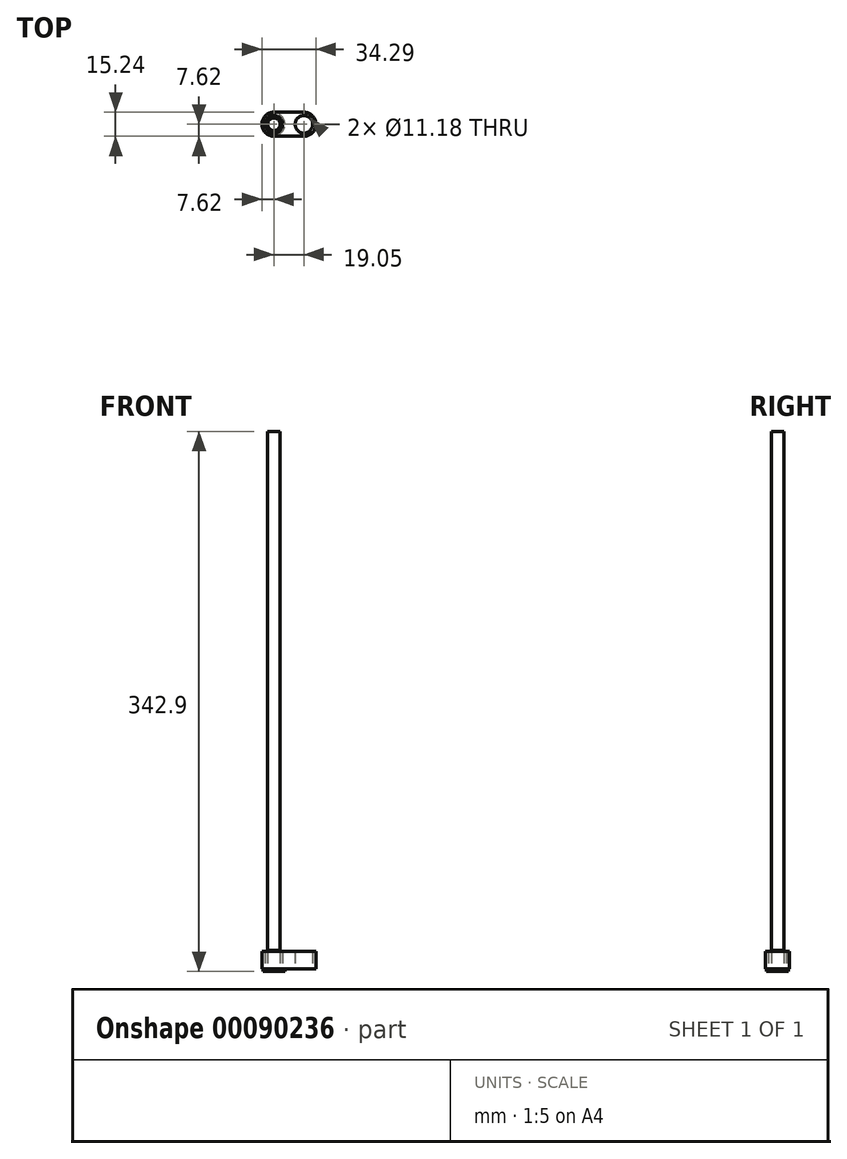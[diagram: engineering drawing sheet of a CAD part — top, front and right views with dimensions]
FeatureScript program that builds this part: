
annotation { "Feature Type Name" : "Feature", "Feature Type Description" : "" }
export const myFeature = defineFeature(function(context is Context, id is Id, definition is map)
    precondition{}
    {
        {
            assignVariable(context, id + "F0", {"name" : "AT", "anyValue" : 0.22});
        }
        {
            var Q0;
            Q0=qCreatedBy(makeId("Top.planeOp"),FACE);
            var sketch = newSketch(context, id + "F1", { "sketchPlane" : qUnion([Q0])});
            skCircle(sketch, "E0", {"center": v(0, 0) * mm, "radius": 3.97 * mm});
            skSolve(sketch);
        }
        {
            var Q0;
            Q0 = qSketchRegion(id + "F1", true);
            extrude(context, id + "F2", {"entities" : qUnion([Q0]), "depth" : 342.9 * mm});
        }
        {
            var Q0;
            Q0=qCreatedBy(makeId("Top.planeOp"),FACE);
            var sketch = newSketch(context, id + "F3", { "sketchPlane" : qUnion([Q0])});
            skCircle(sketch, "E1.0", {"center": v(0, 0) * mm, "radius": 3.97 * mm});
            skCircle(sketch, "E2", {"center": v(0, 0) * mm, "radius": 6.99 * mm});
            skSolve(sketch);
        }
        {
            var Q0;
            Q0=makeQuery(id+"F3.imprint","IMPRINT",FACE,{"disambiguationData":[TD([[makeQuery(id+"F3.imprint","IMPRINT",EDGE,{"derivedFrom":sQuery(id+"F3.wireOp",EDGE,"E1.0")}),-1.0]])]});
            extrude(context, id + "F4", {"entities" : qUnion([Q0]), "depth" : 1.57 * mm});
        }
        {
            var Q0;
            Q0=makeQuery(id+"F4.opExtrude","CAP_FACE",FACE,{"disambiguationData":[OSD([sQuery(id+"F3.wireOp",EDGE,"E1.0"),sQuery(id+"F3.wireOp",EDGE,"E2")])],"isStart":false});
            var sketch = newSketch(context, id + "F5", { "sketchPlane" : qUnion([Q0])});
            skCircle(sketch, "E3.0.0", {"center": v(0, 0) * mm, "radius": 6.99 * mm});
            skCircle(sketch, "E4", {"center": v(0, 0) * mm, "radius": 5.56 * mm});
            skSolve(sketch);
        }
        {
            var Q0;
            Q0=makeQuery(id+"F5.imprint","IMPRINT",FACE,{"disambiguationData":[TD([[makeQuery(id+"F5.imprint","IMPRINT",EDGE,{"derivedFrom":sQuery(id+"F5.wireOp",EDGE,"E4")}),1.0]])]});
            extrude(context, id + "F6", {"entities" : qUnion([Q0]), "operationType" : NewBodyOperationType.ADD, "depth" : 11.05 * mm});
        }
        {
            var Q0;
            Q0=makeQuery(id+"F4.opExtrude","CAP_FACE",FACE,{"disambiguationData":[OSD([sQuery(id+"F3.wireOp",EDGE,"E1.0"),sQuery(id+"F3.wireOp",EDGE,"E2")])],"isStart":false});
            var sketch = newSketch(context, id + "F7", { "sketchPlane" : qUnion([Q0])});
            skCircle(sketch, "E5.0", {"center": v(0, 0) * mm, "radius": 5.56 * mm});
            skCircle(sketch, "E6", {"center": v(0, 0) * mm, "radius": 7.62 * mm});
            skCircle(sketch, "E7", {"center": v(19.05, 0) * mm, "radius": 5.59 * mm});
            skCircle(sketch, "E8", {"center": v(19.05, 0) * mm, "radius": 7.62 * mm});
            skLineSegment(sketch, "E9", {"start": v(0, 7.62) * mm, "end": v(19.05, 7.62) * mm});
            skLineSegment(sketch, "E10", {"start": v(0, -7.62) * mm, "end": v(19.05, -7.62) * mm});
            skCircle(sketch, "E11", {"center": v(0, 0) * mm, "radius": 5.59 * mm});
            skSolve(sketch);
        }
        {
            var Q0;
            Q0=makeQuery(id+"F7.imprint","IMPRINT",FACE,{"disambiguationData":[TD([[makeQuery(id+"F7.imprint","IMPRINT",EDGE,{"derivedFrom":sQuery(id+"F7.wireOp",EDGE,"E11")}),-1.0]])]});
            var Q1;
            Q1=makeQuery(id+"F7.imprint","IMPRINT",FACE,{"disambiguationData":[TD([[makeQuery(id+"F7.imprint","IMPRINT",EDGE,{"derivedFrom":makeQuery(id+"F4.opExtrude","CAP_EDGE",EDGE,{"disambiguationData":[OSD([sQuery(id+"F3.wireOp",EDGE,"E2")])],"isStart":false})}),-1.0]])]});
            var Q2;
            {var subQ0=sQuery(id+"F7.wireOp",EDGE,"E9");Q2=makeQuery(id+"F7.imprint","IMPRINT",FACE,{"disambiguationData":[TD([[makeQuery(id+"F7.imprint","IMPRINT",EDGE,{"derivedFrom":subQ0}),-1.0]])]});}
            var Q3;
            Q3=makeQuery(id+"F7.imprint","IMPRINT",FACE,{"disambiguationData":[TD([[makeQuery(id+"F7.imprint","IMPRINT",EDGE,{"derivedFrom":sQuery(id+"F7.wireOp",EDGE,"E7")}),-1.0]])]});
            var Q4;
            Q4=makeQuery(id+"F6.opExtrude","CAP_FACE",FACE,{"disambiguationData":[OSD([sQuery(id+"F3.wireOp",EDGE,"E1.0"),sQuery(id+"F5.wireOp",EDGE,"E4")])],"isStart":false});
            extrude(context, id + "F8", {"entities" : qUnion([Q0, Q1, Q2, Q3]), "endBound" : BoundingType.UP_TO_SURFACE, "endBoundEntityFace" : qUnion([Q4]), "depth" : 9.4 * mm});
        }
        {
            var Q0;
            Q0=makeQuery(id+"F1.imprint","IMPRINT",FACE,{"disambiguationData":[TD([[makeQuery(id+"F1.imprint","IMPRINT",EDGE,{"derivedFrom":sQuery(id+"F1.wireOp",EDGE,"E0")}),1.0]])]});
            extrude(context, id + "F9", {"entities" : qUnion([Q0]), "depth" : (13 + getVariable(context, 'AT')) * mm});
        }
    });
